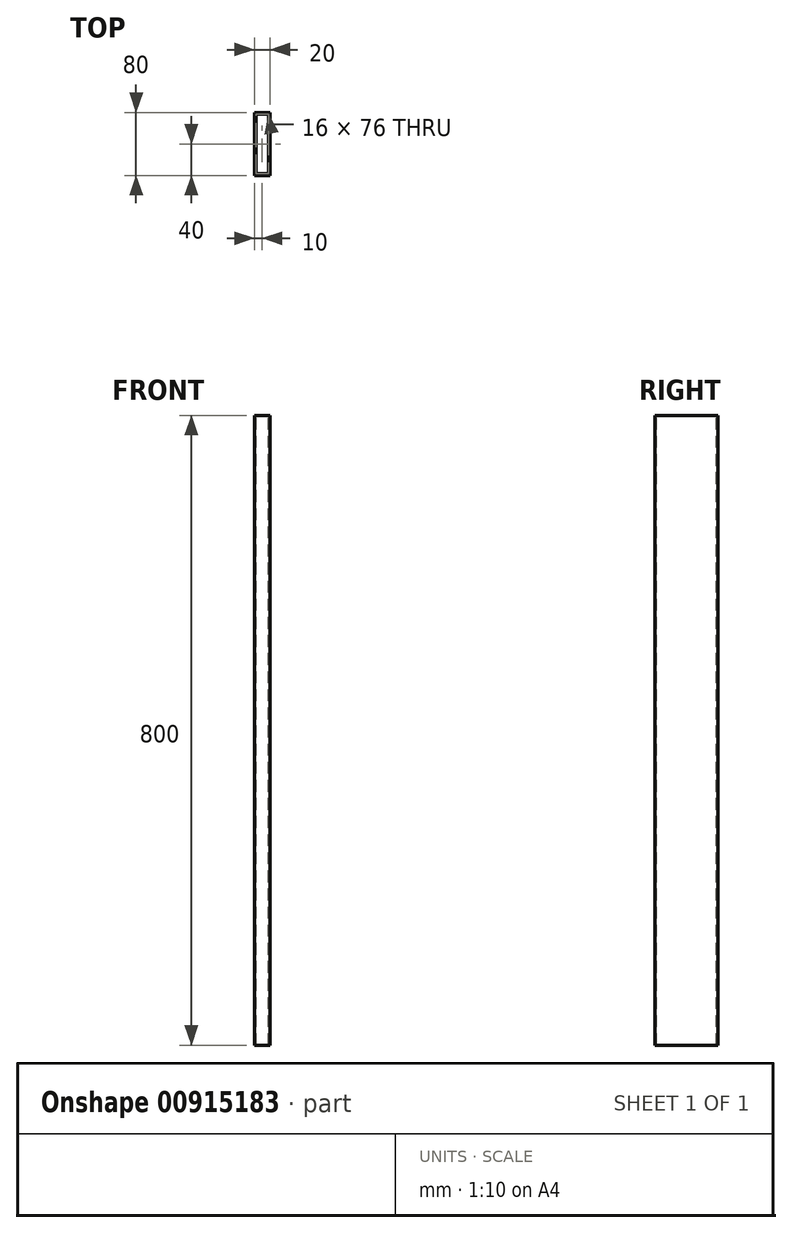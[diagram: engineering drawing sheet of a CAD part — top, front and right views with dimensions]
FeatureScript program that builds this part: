
annotation { "Feature Type Name" : "Feature", "Feature Type Description" : "" }
export const myFeature = defineFeature(function(context is Context, id is Id, definition is map)
    precondition{}
    {
        {
            var Q0;
            Q0=qCreatedBy(makeId("Top.planeOp"),FACE);
            var sketch = newSketch(context, id + "F0", { "sketchPlane" : qUnion([Q0])});
            skLineSegment(sketch, "E0.bottom", {"start": v(0, 40) * mm, "end": v(20, 40) * mm});
            skLineSegment(sketch, "E0.top", {"start": v(0, -40) * mm, "end": v(20, -40) * mm});
            skLineSegment(sketch, "E0.left", {"start": v(0, 40) * mm, "end": v(0, -40) * mm});
            skLineSegment(sketch, "E0.right", {"start": v(20, 40) * mm, "end": v(20, -40) * mm});
            skLineSegment(sketch, "E1.0", {"start": v(2, 38) * mm, "end": v(2, -38) * mm});
            skLineSegment(sketch, "E1.1", {"start": v(2, 38) * mm, "end": v(18, 38) * mm});
            skLineSegment(sketch, "E1.2", {"start": v(18, 38) * mm, "end": v(18, -38) * mm});
            skLineSegment(sketch, "E1.3", {"start": v(2, -38) * mm, "end": v(18, -38) * mm});
            skLineSegment(sketch, "E2.bottom", {"start": v(-3.19, 43.23) * mm, "end": v(22.8, 43.23) * mm, "construction": true});
            skLineSegment(sketch, "E2.top", {"start": v(-3.19, -42.87) * mm, "end": v(22.8, -42.87) * mm, "construction": true});
            skLineSegment(sketch, "E2.left", {"start": v(-3.19, 43.23) * mm, "end": v(-3.19, -42.87) * mm, "construction": true});
            skLineSegment(sketch, "E2.right", {"start": v(22.8, 43.23) * mm, "end": v(22.8, -42.87) * mm, "construction": true});
            skSolve(sketch);
        }
        {
            var Q0;
            Q0 = qSketchRegion(id + "F0", true);
            extrude(context, id + "F1", {"entities" : qUnion([Q0]), "oppositeDirection" : true, "depth" : 800 * mm, "offsetDistance" : 25 * mm});
        }
    });
